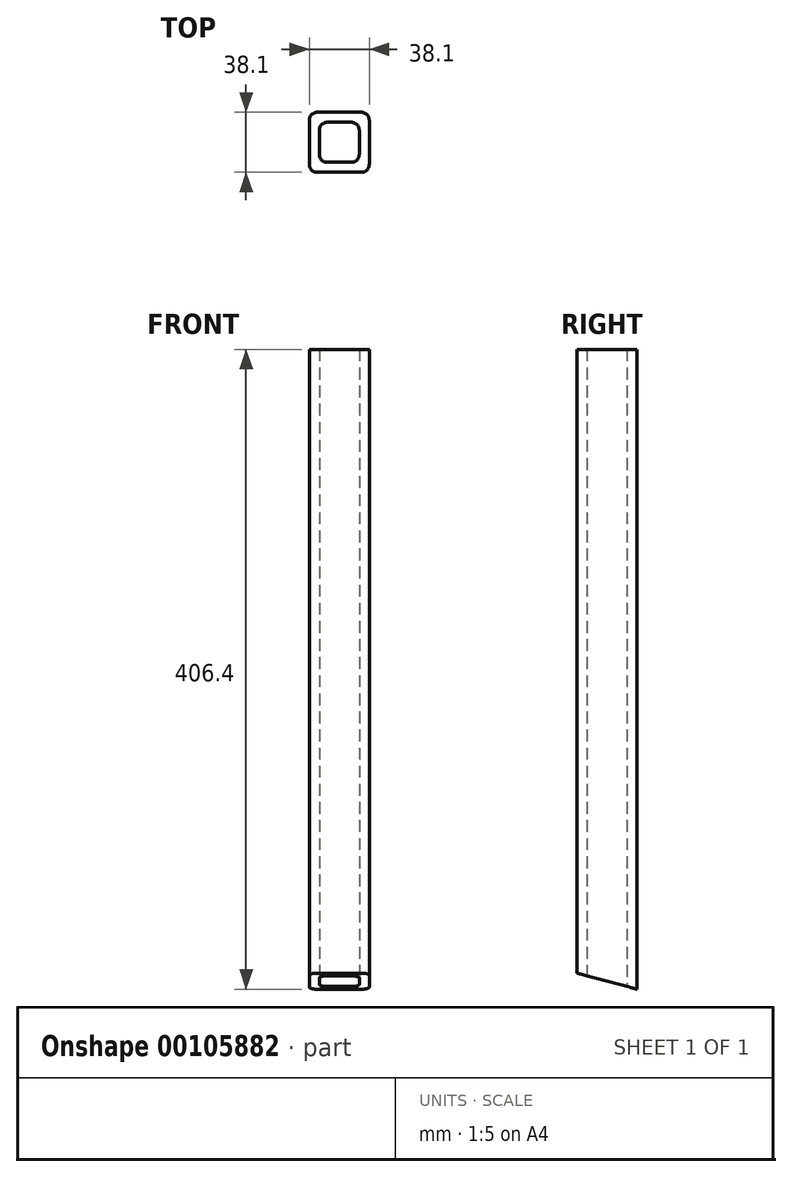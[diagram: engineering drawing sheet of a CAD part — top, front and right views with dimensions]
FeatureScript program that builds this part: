
annotation { "Feature Type Name" : "Feature", "Feature Type Description" : "" }
export const myFeature = defineFeature(function(context is Context, id is Id, definition is map)
    precondition{}
    {
        {
            var Q0;
            Q0=qCreatedBy(makeId("Top.planeOp"),FACE);
            var sketch = newSketch(context, id + "F0", { "sketchPlane" : qUnion([Q0])});
            skLineSegment(sketch, "E0.bottom", {"start": v(19.05, 19.05) * mm, "end": v(-19.05, 19.05) * mm});
            skLineSegment(sketch, "E0.top", {"start": v(19.05, -19.05) * mm, "end": v(-19.05, -19.05) * mm});
            skLineSegment(sketch, "E0.left", {"start": v(19.05, 19.05) * mm, "end": v(19.05, -19.05) * mm});
            skLineSegment(sketch, "E0.right", {"start": v(-19.05, 19.05) * mm, "end": v(-19.05, -19.05) * mm});
            skPoint(sketch, "E0.middle", {"position": v(0, 0) * mm});
            skLineSegment(sketch, "E1.0", {"start": v(12.7, 12.7) * mm, "end": v(-12.7, 12.7) * mm});
            skLineSegment(sketch, "E1.1", {"start": v(12.7, 12.7) * mm, "end": v(12.7, -12.7) * mm});
            skLineSegment(sketch, "E1.2", {"start": v(12.7, -12.7) * mm, "end": v(-12.7, -12.7) * mm});
            skLineSegment(sketch, "E1.3", {"start": v(-12.7, 12.7) * mm, "end": v(-12.7, -12.7) * mm});
            skSolve(sketch);
        }
        {
            var Q0;
            Q0 = qSketchRegion(id + "F0", true);
            extrude(context, id + "F1", {"entities" : qUnion([Q0]), "depth" : 203.2 * mm});
        }
        {
            var Q0;
            Q0=makeQuery(id+"F1.opExtrude","SWEPT_EDGE",EDGE,{"disambiguationData":[OSD([sQuery(id+"F0.wireOp",EDGE,"E0.bottom"),sQuery(id+"F0.wireOp",EDGE,"E0.right")])]});
            var Q1;
            Q1=makeQuery(id+"F1.opExtrude","SWEPT_EDGE",EDGE,{"disambiguationData":[OSD([sQuery(id+"F0.wireOp",EDGE,"E0.top"),sQuery(id+"F0.wireOp",EDGE,"E0.right")])]});
            var Q2;
            Q2=makeQuery(id+"F1.opExtrude","SWEPT_EDGE",EDGE,{"disambiguationData":[OSD([sQuery(id+"F0.wireOp",EDGE,"E0.top"),sQuery(id+"F0.wireOp",EDGE,"E0.left")])]});
            var Q3;
            Q3=makeQuery(id+"F1.opExtrude","SWEPT_EDGE",EDGE,{"disambiguationData":[OSD([sQuery(id+"F0.wireOp",EDGE,"E0.bottom"),sQuery(id+"F0.wireOp",EDGE,"E0.left")])]});
            var Q4;
            Q4=makeQuery(id+"F1.opExtrude","SWEPT_EDGE",EDGE,{"disambiguationData":[OSD([sQuery(id+"F0.wireOp",EDGE,"E1.0"),sQuery(id+"F0.wireOp",EDGE,"E1.3")])]});
            var Q5;
            Q5=makeQuery(id+"F1.opExtrude","SWEPT_EDGE",EDGE,{"disambiguationData":[OSD([sQuery(id+"F0.wireOp",EDGE,"E1.0"),sQuery(id+"F0.wireOp",EDGE,"E1.1")])]});
            var Q6;
            Q6=makeQuery(id+"F1.opExtrude","SWEPT_EDGE",EDGE,{"disambiguationData":[OSD([sQuery(id+"F0.wireOp",EDGE,"E1.1"),sQuery(id+"F0.wireOp",EDGE,"E1.2")])]});
            var Q7;
            Q7=makeQuery(id+"F1.opExtrude","SWEPT_EDGE",EDGE,{"disambiguationData":[OSD([sQuery(id+"F0.wireOp",EDGE,"E1.2"),sQuery(id+"F0.wireOp",EDGE,"E1.3")])]});
            fillet(context, id + "F2", {"entities" : qUnion([Q0, Q1, Q2, Q3, Q4, Q5, Q6, Q7]), "radius" : 5.08 * mm, "tangentPropagation" : true, "allowEdgeOverflow" : false});
        }
        {
            var Q0;
            Q0=makeQuery(id+"F1.opExtrude","SWEPT_BODY",BODY,{"disambiguationData":[OSD([sQuery(id+"F0.wireOp",EDGE,"E0.bottom"),sQuery(id+"F0.wireOp",EDGE,"E0.top"),sQuery(id+"F0.wireOp",EDGE,"E0.left"),sQuery(id+"F0.wireOp",EDGE,"E0.right"),sQuery(id+"F0.wireOp",EDGE,"E1.0"),sQuery(id+"F0.wireOp",EDGE,"E1.1"),sQuery(id+"F0.wireOp",EDGE,"E1.2"),sQuery(id+"F0.wireOp",EDGE,"E1.3")])]});
            var Q1;
            Q1=makeQuery(id+"F1.opExtrude","CAP_FACE",FACE,{"disambiguationData":[OSD([sQuery(id+"F0.wireOp",EDGE,"E0.bottom"),sQuery(id+"F0.wireOp",EDGE,"E0.top"),sQuery(id+"F0.wireOp",EDGE,"E0.left"),sQuery(id+"F0.wireOp",EDGE,"E0.right"),sQuery(id+"F0.wireOp",EDGE,"E1.0"),sQuery(id+"F0.wireOp",EDGE,"E1.1"),sQuery(id+"F0.wireOp",EDGE,"E1.2"),sQuery(id+"F0.wireOp",EDGE,"E1.3")])],"isStart":false});
            mirror(context, id + "F3", {"operationType" : NewBodyOperationType.ADD, "entities" : qUnion([Q0]), "mirrorPlane" : qUnion([Q1])});
        }
        {
            var Q0;
            {var subQ0=makeQuery(id+"F1.opExtrude","SWEPT_FACE",FACE,{"disambiguationData":[OSD([sQuery(id+"F0.wireOp",EDGE,"E0.right")])]});Q0=makeQuery(id+"F3.boolean.opBoolean","MERGE",FACE,{"derivedFrom":[subQ0,makeQuery(id+"F3.opPattern","COPY",FACE,{"derivedFrom":subQ0,"instanceName":"1"})]});}
            var sketch = newSketch(context, id + "F4", { "sketchPlane" : qUnion([Q0])});
            skLineSegment(sketch, "E2", {"start": v(-19.05, 0) * mm, "end": v(19.05, 10.2) * mm});
            skLineSegment(sketch, "E3", {"start": v(19.05, 10.2) * mm, "end": v(19.05, 0) * mm});
            skLineSegment(sketch, "E4", {"start": v(19.05, 0) * mm, "end": v(-19.05, 0) * mm});
            skSolve(sketch);
        }
        {
            var Q0;
            Q0 = qSketchRegion(id + "F4", true);
            var Q1;
            {var subQ0=makeQuery(id+"F1.opExtrude","SWEPT_FACE",FACE,{"disambiguationData":[OSD([sQuery(id+"F0.wireOp",EDGE,"E0.left")])]});Q1=makeQuery(id+"F3.boolean.opBoolean","MERGE",FACE,{"derivedFrom":[subQ0,makeQuery(id+"F3.opPattern","COPY",FACE,{"derivedFrom":subQ0,"instanceName":"1"})]});}
            extrude(context, id + "F5", {"entities" : qUnion([Q0]), "operationType" : NewBodyOperationType.REMOVE, "endBound" : BoundingType.UP_TO_SURFACE, "oppositeDirection" : true, "endBoundEntityFace" : qUnion([Q1]), "depth" : 25.4 * mm});
        }
    });
